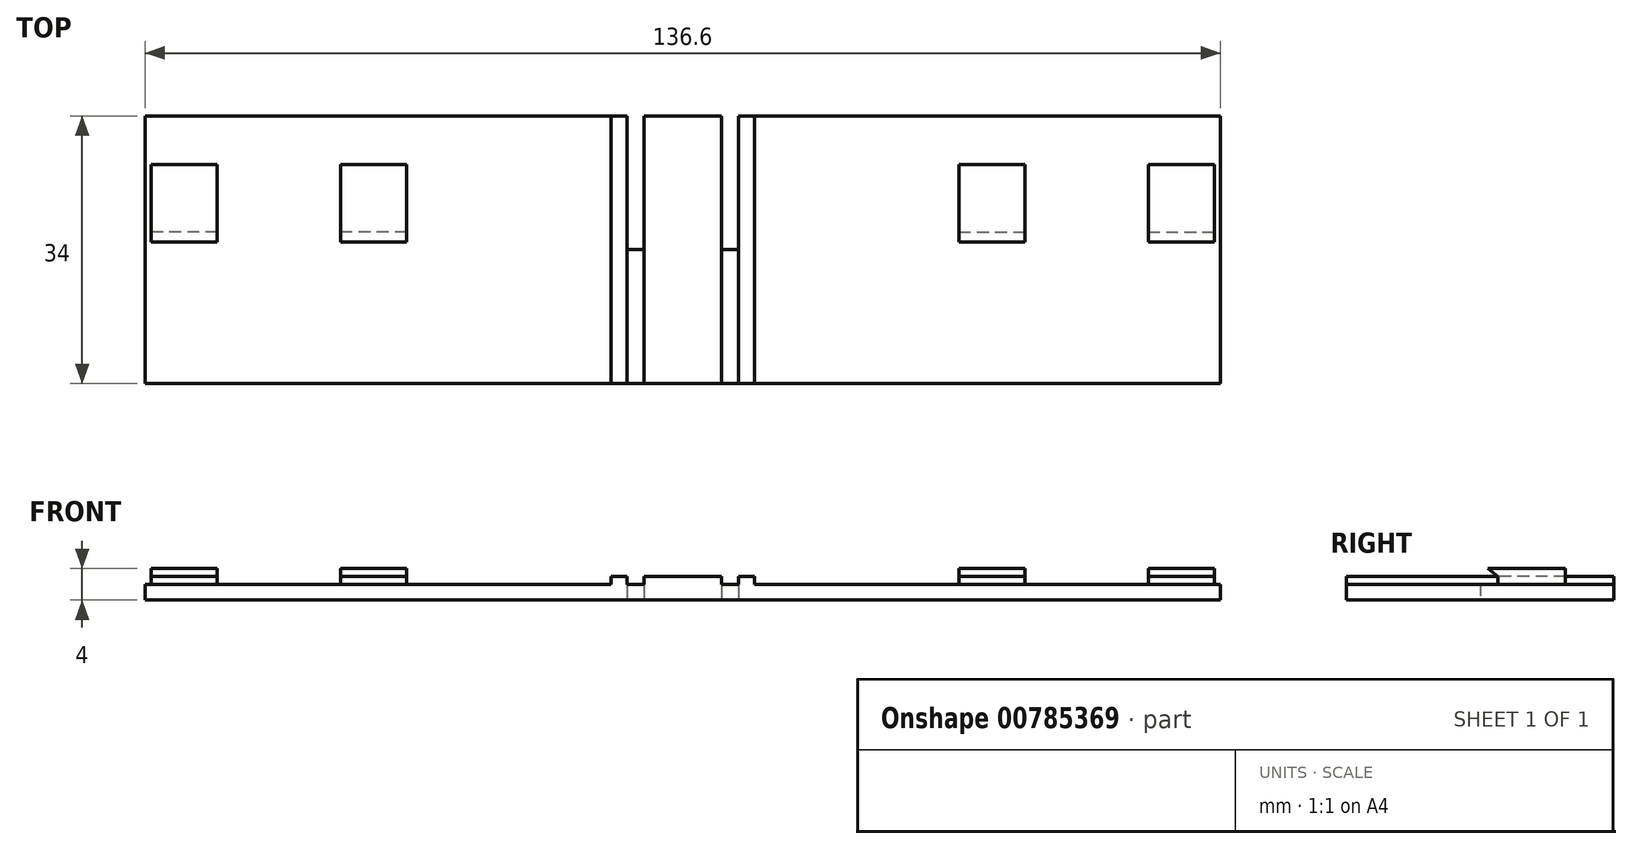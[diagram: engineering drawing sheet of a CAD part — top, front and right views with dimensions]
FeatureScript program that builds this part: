
annotation { "Feature Type Name" : "Feature", "Feature Type Description" : "" }
export const myFeature = defineFeature(function(context is Context, id is Id, definition is map)
    precondition{}
    {
        {
            assignVariable(context, id + "F0", {"name" : "slatthickness", "anyValue" : 2});
        }
        {
            var Q0;
            Q0=qCreatedBy(makeId("Top.planeOp"),FACE);
            var sketch = newSketch(context, id + "F1", { "sketchPlane" : qUnion([Q0])});
            skLineSegment(sketch, "E0", {"start": v(-39.28, 0) * mm, "end": v(39.28, 0) * mm, "construction": true});
            skLineSegment(sketch, "E1.bottom", {"start": v(-35.08, 4.86) * mm, "end": v(-43.48, 4.86) * mm, "construction": true});
            skLineSegment(sketch, "E1.top", {"start": v(-35.08, -4.86) * mm, "end": v(-43.48, -4.86) * mm, "construction": true});
            skLineSegment(sketch, "E1.left", {"start": v(-35.08, 4.86) * mm, "end": v(-35.08, -4.86) * mm, "construction": true});
            skLineSegment(sketch, "E1.right", {"start": v(-43.48, 4.86) * mm, "end": v(-43.48, -4.86) * mm, "construction": true});
            skPoint(sketch, "E1.middle", {"position": v(-39.28, 0) * mm});
            skLineSegment(sketch, "E2", {"start": v(-39.28, 0) * mm, "end": v(-63.32, 0) * mm, "construction": true});
            skLineSegment(sketch, "E3.bottom", {"start": v(-59.12, 4.86) * mm, "end": v(-67.53, 4.86) * mm, "construction": true});
            skLineSegment(sketch, "E3.top", {"start": v(-59.12, -4.86) * mm, "end": v(-67.53, -4.86) * mm, "construction": true});
            skLineSegment(sketch, "E3.left", {"start": v(-59.12, 4.86) * mm, "end": v(-59.12, -4.86) * mm, "construction": true});
            skLineSegment(sketch, "E3.right", {"start": v(-67.53, 4.86) * mm, "end": v(-67.53, -4.86) * mm, "construction": true});
            skPoint(sketch, "E3.middle", {"position": v(-63.32, 0) * mm});
            skLineSegment(sketch, "E4", {"start": v(0, 9.87) * mm, "end": v(0, -24.13) * mm, "construction": true});
            skLineSegment(sketch, "E5.bottom", {"start": v(-68.3, 9.87) * mm, "end": v(68.3, 9.87) * mm});
            skLineSegment(sketch, "E5.top", {"start": v(-68.3, -24.13) * mm, "end": v(68.3, -24.13) * mm});
            skLineSegment(sketch, "E5.left", {"start": v(-68.3, 9.87) * mm, "end": v(-68.3, -24.13) * mm});
            skLineSegment(sketch, "E5.right", {"start": v(68.3, 9.87) * mm, "end": v(68.3, -24.13) * mm});
            skPoint(sketch, "E5.middle", {"position": v(0, -7.13) * mm});
            skPoint(sketch, "E6", {"position": v(-51.3, 0) * mm});
            skLineSegment(sketch, "E7.MirrorCS", {"start": v(35.08, -4.86) * mm, "end": v(43.48, -4.86) * mm, "construction": true});
            skLineSegment(sketch, "E8.MirrorCS", {"start": v(35.08, 4.86) * mm, "end": v(35.08, -4.86) * mm, "construction": true});
            skLineSegment(sketch, "E9.MirrorCS", {"start": v(35.08, 4.86) * mm, "end": v(43.48, 4.86) * mm, "construction": true});
            skLineSegment(sketch, "E10.MirrorCS", {"start": v(43.48, 4.86) * mm, "end": v(43.48, -4.86) * mm, "construction": true});
            skLineSegment(sketch, "E11.MirrorCS", {"start": v(59.12, 4.86) * mm, "end": v(59.12, -4.86) * mm, "construction": true});
            skLineSegment(sketch, "E12.MirrorCS", {"start": v(59.12, 4.86) * mm, "end": v(67.53, 4.86) * mm, "construction": true});
            skLineSegment(sketch, "E13.MirrorCS", {"start": v(67.53, 4.86) * mm, "end": v(67.53, -4.86) * mm, "construction": true});
            skLineSegment(sketch, "E14.MirrorCS", {"start": v(59.12, -4.86) * mm, "end": v(67.53, -4.86) * mm, "construction": true});
            skLineSegment(sketch, "E15", {"start": v(-4.93, -7.13) * mm, "end": v(4.94, -7.13) * mm, "construction": true});
            skLineSegment(sketch, "E16.bottom", {"start": v(-4.93, -7.13) * mm, "end": v(-7.08, -7.13) * mm});
            skLineSegment(sketch, "E16.top", {"start": v(-4.94, 9.87) * mm, "end": v(-7.08, 9.87) * mm});
            skLineSegment(sketch, "E16.left", {"start": v(-4.93, -7.13) * mm, "end": v(-4.94, 9.87) * mm});
            skLineSegment(sketch, "E16.right", {"start": v(-7.08, -7.13) * mm, "end": v(-7.08, 9.87) * mm});
            skLineSegment(sketch, "E17.MirrorCS", {"start": v(4.93, -7.13) * mm, "end": v(4.94, 9.87) * mm});
            skLineSegment(sketch, "E18.MirrorCS", {"start": v(4.93, -7.13) * mm, "end": v(7.08, -7.13) * mm});
            skLineSegment(sketch, "E19.MirrorCS", {"start": v(7.08, -7.13) * mm, "end": v(7.08, 9.87) * mm});
            skSolve(sketch);
        }
        {
            var Q0;
            Q0=makeQuery(id+"F1.imprint","IMPRINT",FACE,{"disambiguationData":[TD([[makeQuery(id+"F1.imprint","IMPRINT",EDGE,{"derivedFrom":sQuery(id+"F1.wireOp",EDGE,"E5.top")}),1.0]])]});
            extrude(context, id + "F2", {"entities" : qUnion([Q0]), "depth" : (getVariable(context, 'slatthickness')) * mm, "offsetDistance" : 25 * mm});
        }
        {
            var Q0;
            Q0=makeQuery(id+"F2.opExtrude","CAP_FACE",FACE,{"disambiguationData":[OSD([sQuery(id+"F1.wireOp",EDGE,"E5.bottom"),sQuery(id+"F1.wireOp",EDGE,"E5.top"),sQuery(id+"F1.wireOp",EDGE,"E5.left"),sQuery(id+"F1.wireOp",EDGE,"E5.right")])],"isStart":false});
            var sketch = newSketch(context, id + "F3", { "sketchPlane" : qUnion([Q0])});
            skLineSegment(sketch, "E20.0", {"start": v(-59.12, 4.86) * mm, "end": v(-67.53, 4.86) * mm});
            skLineSegment(sketch, "E21.0", {"start": v(-59.12, 4.86) * mm, "end": v(-59.12, -4.86) * mm});
            skLineSegment(sketch, "E22.0", {"start": v(-59.12, -4.86) * mm, "end": v(-67.53, -4.86) * mm});
            skLineSegment(sketch, "E23.0", {"start": v(-67.53, 4.86) * mm, "end": v(-67.53, -4.86) * mm});
            skLineSegment(sketch, "E24.0", {"start": v(-43.48, 4.86) * mm, "end": v(-43.48, -4.86) * mm});
            skLineSegment(sketch, "E25.0", {"start": v(-35.08, 4.86) * mm, "end": v(-43.48, 4.86) * mm});
            skLineSegment(sketch, "E26.0", {"start": v(-35.08, 4.86) * mm, "end": v(-35.08, -4.86) * mm});
            skLineSegment(sketch, "E27.0", {"start": v(-35.08, -4.86) * mm, "end": v(-43.48, -4.86) * mm});
            skLineSegment(sketch, "E28.0", {"start": v(35.08, 4.86) * mm, "end": v(35.08, -4.86) * mm});
            skLineSegment(sketch, "E29.0", {"start": v(35.08, 4.86) * mm, "end": v(43.48, 4.86) * mm});
            skLineSegment(sketch, "E30.0", {"start": v(35.08, -4.86) * mm, "end": v(43.48, -4.86) * mm});
            skLineSegment(sketch, "E31.0", {"start": v(43.48, 4.86) * mm, "end": v(43.48, -4.86) * mm});
            skLineSegment(sketch, "E32.0", {"start": v(59.12, 4.86) * mm, "end": v(59.12, -4.86) * mm});
            skLineSegment(sketch, "E33.0", {"start": v(59.12, 4.86) * mm, "end": v(67.53, 4.86) * mm});
            skLineSegment(sketch, "E34.0", {"start": v(67.53, 4.86) * mm, "end": v(67.53, -4.86) * mm});
            skLineSegment(sketch, "E35.0", {"start": v(59.12, -4.86) * mm, "end": v(67.53, -4.86) * mm});
            skSolve(sketch);
        }
        {
            var Q0;
            Q0 = qSketchRegion(id + "F3", true);
            extrude(context, id + "F4", {"entities" : qUnion([Q0]), "operationType" : NewBodyOperationType.ADD, "depth" : (getVariable(context, 'slatthickness')) * mm, "offsetDistance" : 25 * mm});
        }
        {
            var Q0;
            Q0=makeQuery(id+"F4.opExtrude","SWEPT_FACE",FACE,{"disambiguationData":[OSD([sQuery(id+"F3.wireOp",EDGE,"E23.0")])]});
            var sketch = newSketch(context, id + "F5", { "sketchPlane" : qUnion([Q0])});
            skLineSegment(sketch, "E36", {"start": v(4.86, 4) * mm, "end": v(6.16, 4) * mm});
            skLineSegment(sketch, "E37", {"start": v(6.16, 4) * mm, "end": v(4.86, 3) * mm});
            skLineSegment(sketch, "E38", {"start": v(4.86, 3) * mm, "end": v(4.86, 4) * mm});
            skSolve(sketch);
        }
        {
            var Q0;
            Q0 = qSketchRegion(id + "F5", true);
            var Q1;
            Q1=makeQuery(id+"F4.opExtrude","SWEPT_FACE",FACE,{"disambiguationData":[OSD([sQuery(id+"F3.wireOp",EDGE,"E34.0")])]});
            extrude(context, id + "F6", {"entities" : qUnion([Q0]), "operationType" : NewBodyOperationType.ADD, "endBound" : BoundingType.UP_TO_SURFACE, "oppositeDirection" : true, "depth" : 25 * mm, "endBoundEntityFace" : qUnion([Q1]), "offsetDistance" : 25 * mm});
        }
        {
            var Q0;
            {var subQ2=sQuery(id+"F3.wireOp",EDGE,"E21.0");Q0=makeQuery(id+"F6.boolean.opBoolean","SPLIT",FACE,{"disambiguationData":[TD([makeQuery(id+"F4.opExtrude","SWEPT_FACE",FACE,{"disambiguationData":[OSD([subQ2])]})])],"derivedFrom":makeQuery(id+"F6.opExtrude","SWEPT_FACE",FACE,{"disambiguationData":[OSD([sQuery(id+"F5.wireOp",EDGE,"E38")])]})});}
            var Q1;
            {var subQ1=sQuery(id+"F3.wireOp",EDGE,"E26.0");Q1=makeQuery(id+"F6.boolean.opBoolean","SPLIT",FACE,{"disambiguationData":[TD([makeQuery(id+"F4.opExtrude","SWEPT_FACE",FACE,{"disambiguationData":[OSD([subQ1])]})])],"derivedFrom":makeQuery(id+"F6.opExtrude","SWEPT_FACE",FACE,{"disambiguationData":[OSD([sQuery(id+"F5.wireOp",EDGE,"E38")])]})});}
            var Q2;
            {var subQ1=sQuery(id+"F3.wireOp",EDGE,"E31.0");Q2=makeQuery(id+"F6.boolean.opBoolean","SPLIT",FACE,{"disambiguationData":[TD([makeQuery(id+"F4.opExtrude","SWEPT_FACE",FACE,{"disambiguationData":[OSD([subQ1])]})])],"derivedFrom":makeQuery(id+"F6.opExtrude","SWEPT_FACE",FACE,{"disambiguationData":[OSD([sQuery(id+"F5.wireOp",EDGE,"E38")])]})});}
            extrude(context, id + "F7", {"entities" : qUnion([Q0, Q1, Q2]), "operationType" : NewBodyOperationType.REMOVE, "endBound" : BoundingType.THROUGH_ALL, "oppositeDirection" : true, "depth" : 25 * mm, "offsetDistance" : 25 * mm});
        }
        {
            var Q0;
            Q0=makeQuery(id+"F2.opExtrude","CAP_FACE",FACE,{"disambiguationData":[OSD([sQuery(id+"F1.wireOp",EDGE,"E5.bottom"),sQuery(id+"F1.wireOp",EDGE,"E5.top"),sQuery(id+"F1.wireOp",EDGE,"E5.left"),sQuery(id+"F1.wireOp",EDGE,"E5.right"),sQuery(id+"F1.wireOp",EDGE,"E16.bottom"),sQuery(id+"F1.wireOp",EDGE,"E16.left"),sQuery(id+"F1.wireOp",EDGE,"E16.right"),sQuery(id+"F1.wireOp",EDGE,"E17.MirrorCS"),sQuery(id+"F1.wireOp",EDGE,"E18.MirrorCS"),sQuery(id+"F1.wireOp",EDGE,"E19.MirrorCS")])],"isStart":false});
            var sketch = newSketch(context, id + "F8", { "sketchPlane" : qUnion([Q0])});
            skLineSegment(sketch, "E39.bottom", {"start": v(-4.94, 9.87) * mm, "end": v(4.93, 9.87) * mm});
            skLineSegment(sketch, "E39.top", {"start": v(-4.94, -24.13) * mm, "end": v(4.93, -24.13) * mm});
            skLineSegment(sketch, "E39.left", {"start": v(-4.94, 9.87) * mm, "end": v(-4.94, -24.13) * mm});
            skLineSegment(sketch, "E39.right", {"start": v(4.93, 9.87) * mm, "end": v(4.93, -24.13) * mm});
            skLineSegment(sketch, "E40.bottom", {"start": v(-7.08, 9.87) * mm, "end": v(-9.09, 9.87) * mm});
            skLineSegment(sketch, "E40.top", {"start": v(-7.08, -24.13) * mm, "end": v(-9.08, -24.13) * mm});
            skLineSegment(sketch, "E40.left", {"start": v(-7.08, 9.87) * mm, "end": v(-7.08, -24.13) * mm});
            skLineSegment(sketch, "E40.right", {"start": v(-9.09, 9.87) * mm, "end": v(-9.08, -24.13) * mm});
            skLineSegment(sketch, "E41.bottom", {"start": v(7.08, 9.87) * mm, "end": v(9.08, 9.87) * mm});
            skLineSegment(sketch, "E41.top", {"start": v(7.08, -24.13) * mm, "end": v(9.09, -24.13) * mm});
            skLineSegment(sketch, "E41.left", {"start": v(7.08, 9.87) * mm, "end": v(7.08, -24.13) * mm});
            skLineSegment(sketch, "E41.right", {"start": v(9.08, 9.87) * mm, "end": v(9.09, -24.13) * mm});
            skSolve(sketch);
        }
        {
            var Q0;
            Q0 = qSketchRegion(id + "F8", true);
            extrude(context, id + "F9", {"entities" : qUnion([Q0]), "operationType" : NewBodyOperationType.ADD, "depth" : 1 * mm, "offsetDistance" : 25 * mm});
        }
        {
            var Q0;
            {var subQ1=sQuery(id+"F5.wireOp",EDGE,"E36");var subQ2=sQuery(id+"F3.wireOp",EDGE,"E21.0");var subQ3=sQuery(id+"F3.wireOp",EDGE,"E23.0");var subQ4=sQuery(id+"F3.wireOp",EDGE,"E20.0");var subQ5=sQuery(id+"F3.wireOp",EDGE,"E22.0");Q0=makeQuery(id+"F7.boolean.opBoolean","SPLIT",FACE,{"disambiguationData":[TD([makeQuery(id+"F4.opExtrude","SWEPT_FACE",FACE,{"disambiguationData":[OSD([subQ4])]})])],"derivedFrom":makeQuery(id+"F6.boolean.opBoolean","MERGE",FACE,{"derivedFrom":[makeQuery(id+"F4.opExtrude","CAP_FACE",FACE,{"disambiguationData":[OSD([subQ4,subQ2,subQ5,subQ3])],"isStart":false}),makeQuery(id+"F4.opExtrude","CAP_FACE",FACE,{"disambiguationData":[OSD([sQuery(id+"F3.wireOp",EDGE,"E24.0"),sQuery(id+"F3.wireOp",EDGE,"E25.0"),sQuery(id+"F3.wireOp",EDGE,"E26.0"),sQuery(id+"F3.wireOp",EDGE,"E27.0")])],"isStart":false}),makeQuery(id+"F4.opExtrude","CAP_FACE",FACE,{"disambiguationData":[OSD([sQuery(id+"F3.wireOp",EDGE,"E28.0"),sQuery(id+"F3.wireOp",EDGE,"E29.0"),sQuery(id+"F3.wireOp",EDGE,"E30.0"),sQuery(id+"F3.wireOp",EDGE,"E31.0")])],"isStart":false}),makeQuery(id+"F4.opExtrude","CAP_FACE",FACE,{"disambiguationData":[OSD([sQuery(id+"F3.wireOp",EDGE,"E32.0"),sQuery(id+"F3.wireOp",EDGE,"E33.0"),sQuery(id+"F3.wireOp",EDGE,"E34.0"),sQuery(id+"F3.wireOp",EDGE,"E35.0")])],"isStart":false}),makeQuery(id+"F6.opExtrude","SWEPT_FACE",FACE,{"disambiguationData":[OSD([subQ1])]})]})});}
            var sketch = newSketch(context, id + "F10", { "sketchPlane" : qUnion([Q0])});
            skLineSegment(sketch, "E42.bottom", {"start": v(-67.53, 4.86) * mm, "end": v(-59.12, 4.86) * mm});
            skLineSegment(sketch, "E42.top", {"start": v(-67.53, 3.71) * mm, "end": v(-59.12, 3.71) * mm});
            skLineSegment(sketch, "E42.left", {"start": v(-67.53, 4.86) * mm, "end": v(-67.53, 3.71) * mm});
            skLineSegment(sketch, "E42.right", {"start": v(-59.12, 4.86) * mm, "end": v(-59.12, 3.71) * mm});
            skPoint(sketch, "E43.0", {"position": v(-51.3, 0) * mm});
            skLineSegment(sketch, "E44", {"start": v(-51.3, 4.86) * mm, "end": v(-51.3, 0) * mm, "construction": true});
            skLineSegment(sketch, "E45.MirrorCS", {"start": v(-43.48, 4.86) * mm, "end": v(-43.48, 3.71) * mm});
            skLineSegment(sketch, "E46.MirrorCS", {"start": v(-35.07, 4.86) * mm, "end": v(-35.07, 3.71) * mm});
            skLineSegment(sketch, "E47.MirrorCS", {"start": v(-35.07, 3.71) * mm, "end": v(-43.48, 3.71) * mm});
            skLineSegment(sketch, "E48.MirrorCS", {"start": v(-35.07, 4.86) * mm, "end": v(-43.48, 4.86) * mm});
            skLineSegment(sketch, "E49.MirrorCS", {"start": v(67.53, 4.86) * mm, "end": v(67.53, 3.71) * mm});
            skLineSegment(sketch, "E50.MirrorCS", {"start": v(43.48, 4.86) * mm, "end": v(43.48, 3.71) * mm});
            skLineSegment(sketch, "E51.MirrorCS", {"start": v(35.07, 4.86) * mm, "end": v(35.07, 3.71) * mm});
            skLineSegment(sketch, "E52.MirrorCS", {"start": v(59.12, 4.86) * mm, "end": v(59.12, 3.71) * mm});
            skLineSegment(sketch, "E53.MirrorCS", {"start": v(35.07, 4.86) * mm, "end": v(43.48, 4.86) * mm});
            skLineSegment(sketch, "E54.MirrorCS", {"start": v(35.07, 3.71) * mm, "end": v(43.48, 3.71) * mm});
            skLineSegment(sketch, "E55.MirrorCS", {"start": v(67.53, 4.86) * mm, "end": v(59.12, 4.86) * mm});
            skLineSegment(sketch, "E56.MirrorCS", {"start": v(67.53, 3.71) * mm, "end": v(59.12, 3.71) * mm});
            skLineSegment(sketch, "E57.MirrorCS", {"start": v(51.3, 4.86) * mm, "end": v(51.3, 0) * mm, "construction": true});
            skSolve(sketch);
        }
        {
            var Q0;
            Q0 = qSketchRegion(id + "F10", true);
            var Q1;
            {var subQ4=sQuery(id+"F1.wireOp",EDGE,"E5.left");var subQ5=sQuery(id+"F1.wireOp",EDGE,"E5.bottom");var subQ6=sQuery(id+"F1.wireOp",EDGE,"E16.right");var subQ8=sQuery(id+"F1.wireOp",EDGE,"E5.top");Q1=makeQuery(id+"F9.boolean.opBoolean","SPLIT",FACE,{"disambiguationData":[TD([makeQuery(id+"F2.opExtrude","SWEPT_FACE",FACE,{"disambiguationData":[OSD([subQ4])]})])],"derivedFrom":makeQuery(id+"F2.opExtrude","CAP_FACE",FACE,{"disambiguationData":[OSD([subQ5,subQ8,subQ4,sQuery(id+"F1.wireOp",EDGE,"E5.right"),sQuery(id+"F1.wireOp",EDGE,"E16.bottom"),sQuery(id+"F1.wireOp",EDGE,"E16.left"),subQ6,sQuery(id+"F1.wireOp",EDGE,"E17.MirrorCS"),sQuery(id+"F1.wireOp",EDGE,"E18.MirrorCS"),sQuery(id+"F1.wireOp",EDGE,"E19.MirrorCS")])],"isStart":false})});}
            extrude(context, id + "F11", {"entities" : qUnion([Q0]), "operationType" : NewBodyOperationType.REMOVE, "endBound" : BoundingType.UP_TO_SURFACE, "oppositeDirection" : true, "depth" : 25 * mm, "endBoundEntityFace" : qUnion([Q1]), "offsetDistance" : 25 * mm});
        }
    });
